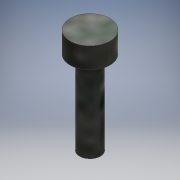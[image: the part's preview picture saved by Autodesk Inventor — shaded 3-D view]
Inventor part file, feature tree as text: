
AUTODESK INVENTOR PART (.ipt)
format: ipt  version: 2016 (Build 200138000, 138)  size: 103,424 bytes
history: native  units: mm
features: extrude x2, other x1, sketch x1
ambient origin geometry x8: Origin, YZ Plane, XZ Plane, XY Plane, X Axis, Y Axis, Z Axis, Center Point
bodies: Body1 (feature_tree)
feature tree (4):
  other  "ソリッド1"
  sketch  "スケッチ1"
  extrude  "押し出し1"  Depth=3.8mm
  extrude  "押し出し2"  Depth=2.0mm
